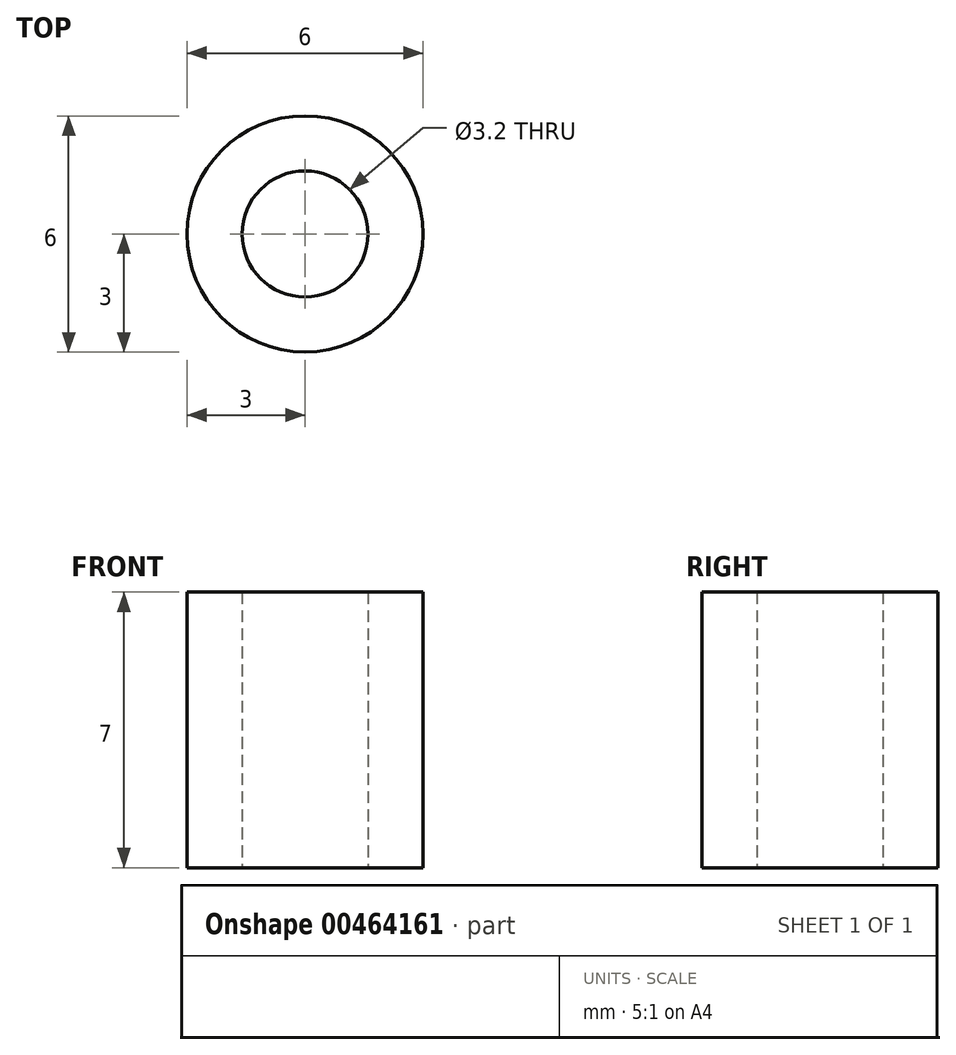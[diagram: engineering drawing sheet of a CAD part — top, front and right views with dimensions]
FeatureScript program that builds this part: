
annotation { "Feature Type Name" : "Feature", "Feature Type Description" : "" }
export const myFeature = defineFeature(function(context is Context, id is Id, definition is map)
    precondition{}
    {
        {
            var Q0;
            Q0=qCreatedBy(makeId("Top.planeOp"),FACE);
            var sketch = newSketch(context, id + "F0", { "sketchPlane" : qUnion([Q0])});
            skCircle(sketch, "E0", {"center": v(0, 0) * mm, "radius": 3 * mm});
            skCircle(sketch, "E1", {"center": v(0, 0) * mm, "radius": 1.6 * mm});
            skSolve(sketch);
        }
        {
            var Q0;
            Q0 = qSketchRegion(id + "F0", true);
            extrude(context, id + "F1", {"entities" : qUnion([Q0]), "depth" : 7 * mm});
        }
    });
